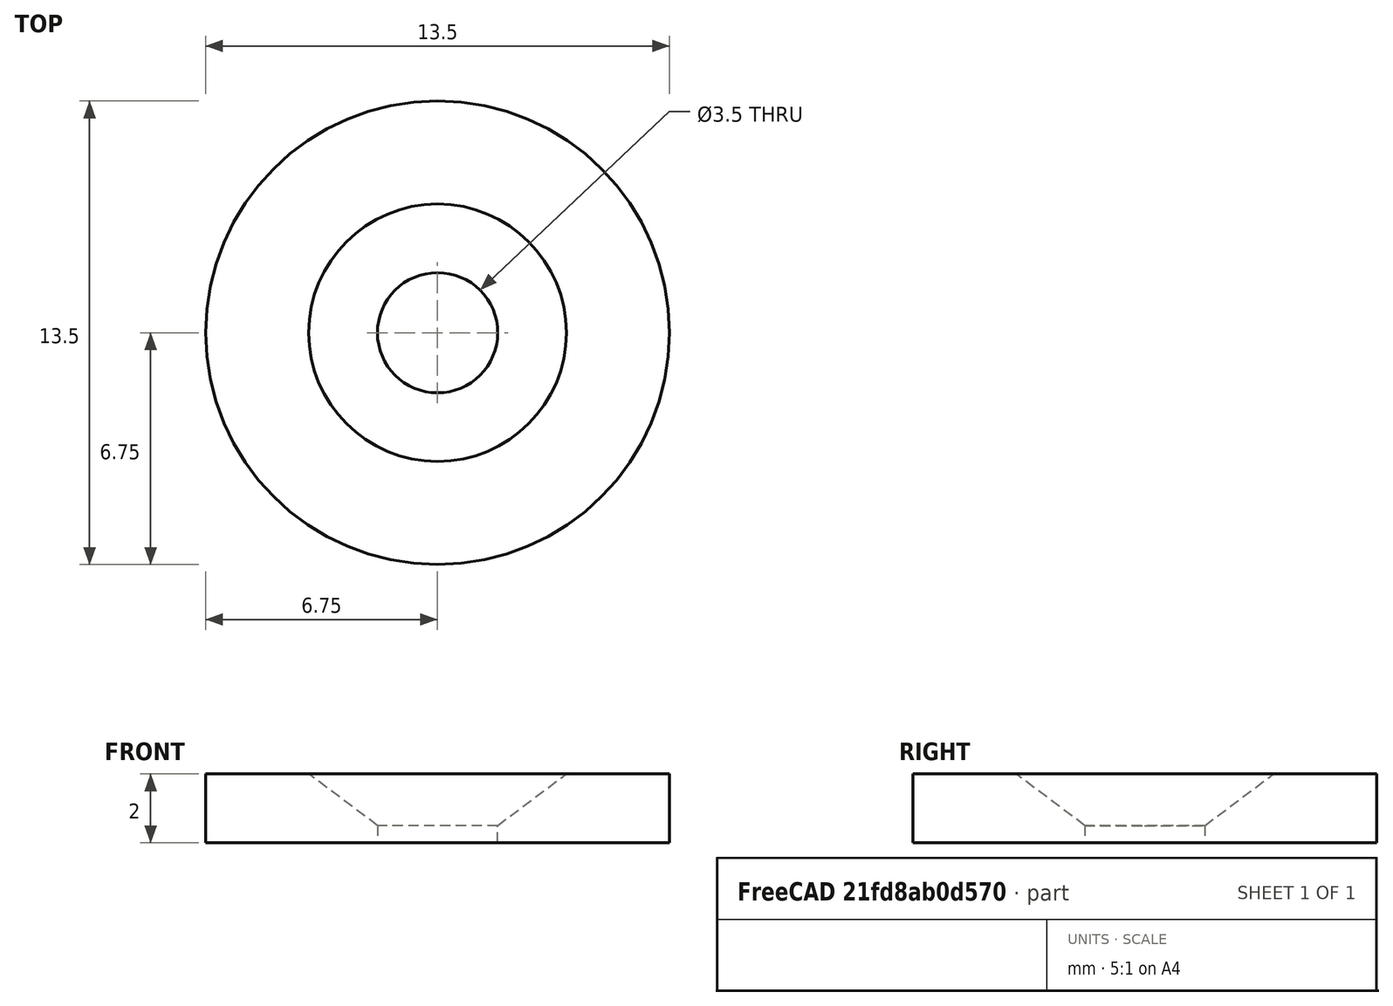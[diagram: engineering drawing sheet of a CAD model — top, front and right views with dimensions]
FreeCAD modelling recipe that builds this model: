
FCSTD DOCUMENT  (FreeCAD 0.19R)
Label: puzzle-mat-clamp
License: All rights reserved
LicenseURL: http://en.wikipedia.org/wiki/All_rights_reserved
objects: Sketcher::SketchObject×1, PartDesign::Pad×1, PartDesign::Chamfer×1, PartDesign::Body×1
note: 6 computed .brp shape members not serialized (recipe doc carries the construction recipe); baked Part::Feature solids carry a one-line shape summary decoded from their .brp

FEATURE [Sketcher::SketchObject] Sketch
  FullyConstrained = true
  MapMode = 5
  Support = -> [XY_Plane]
  sketch-geometry (2):
    g0: Circle CenterX=0 CenterY=0 CenterZ=0 NormalX=0 NormalY=0 NormalZ=1 AngleXU=0 Radius=1.75
    g1: Circle CenterX=0 CenterY=0 CenterZ=0 NormalX=0 NormalY=0 NormalZ=1 AngleXU=0 Radius=6.75
  constraints (4):
    c: Coincident(g0,g-1)
    c: Coincident(g1,g0)
    c: Diameter(g1) = 13.5
    c: Diameter(g0) = 3.5
FEATURE [PartDesign::Pad] Pad
  Direction = (1,1,1)
  Length = 2
  Length2 = 100
  Profile = -> Sketch
  Type = 0
FEATURE [PartDesign::Chamfer] Chamfer
  Angle = 45
  Base = -> Pad [Edge6]
  BaseFeature = -> Pad
  ChamferType = 1
  FlipDirection = false
  Size = 1.5
  Size2 = 2
  SupportTransform = false
FEATURE [PartDesign::Body] Body
  Group = -> [Sketch,Pad,Chamfer]
  Origin = -> Origin
  Tip = -> Chamfer
